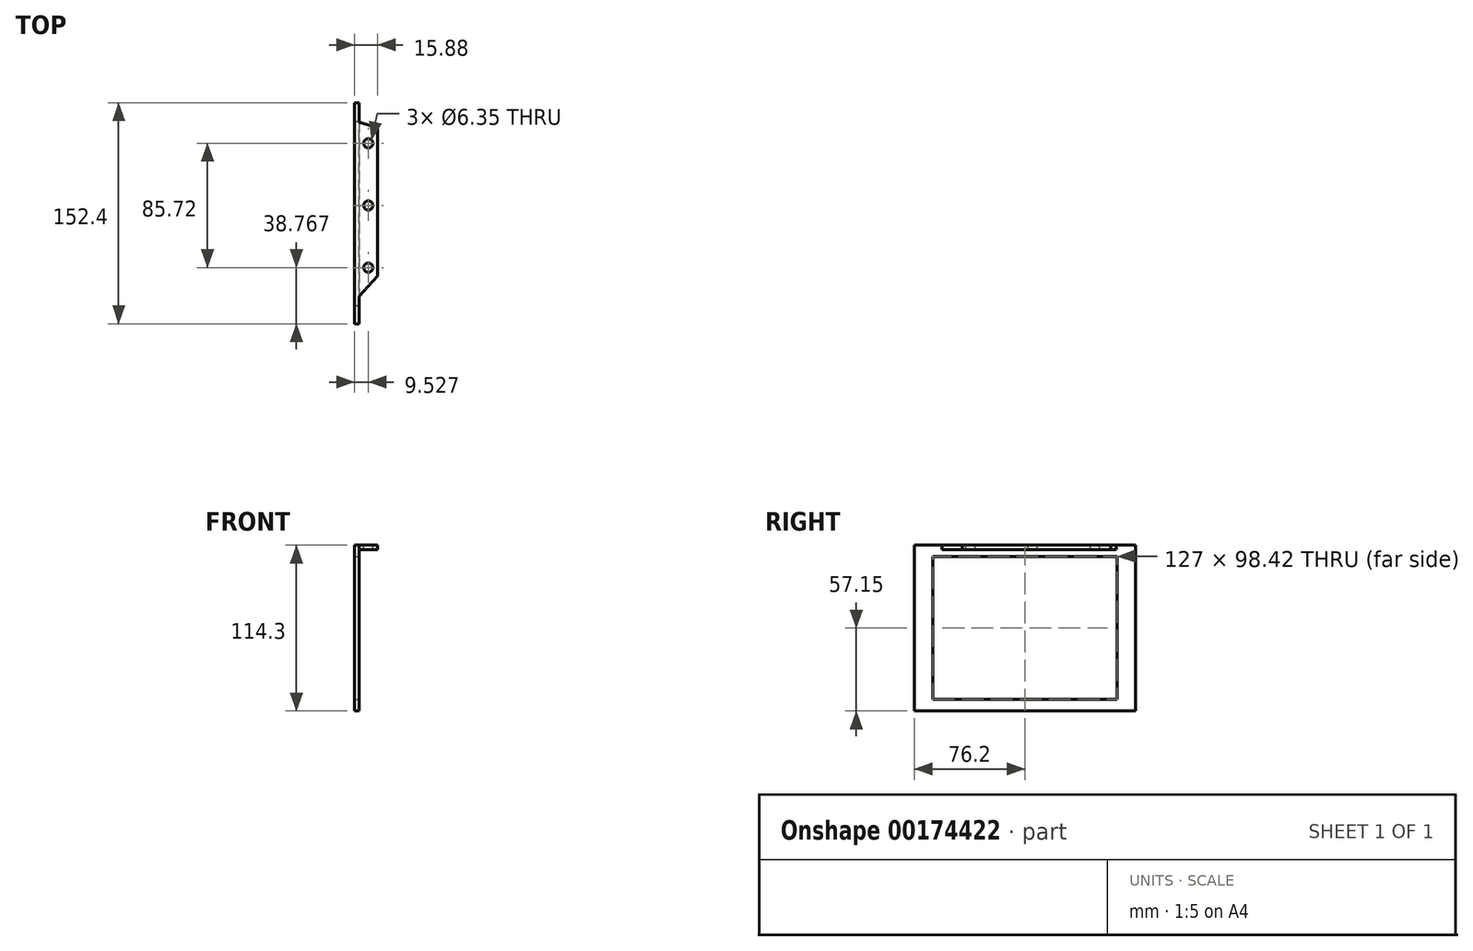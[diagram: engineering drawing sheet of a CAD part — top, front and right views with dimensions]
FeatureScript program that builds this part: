
annotation { "Feature Type Name" : "Feature", "Feature Type Description" : "" }
export const myFeature = defineFeature(function(context is Context, id is Id, definition is map)
    precondition{}
    {
        {
            var Q0;
            Q0=qCreatedBy(makeId("Top.planeOp"),FACE);
            var sketch = newSketch(context, id + "F0", { "sketchPlane" : qUnion([Q0])});
            skLineSegment(sketch, "E0.bottom", {"start": v(1.59, -76.2) * mm, "end": v(-1.59, -76.2) * mm});
            skLineSegment(sketch, "E0.top", {"start": v(1.59, 76.2) * mm, "end": v(-1.59, 76.2) * mm});
            skLineSegment(sketch, "E0.left", {"start": v(1.59, -76.2) * mm, "end": v(1.59, 76.2) * mm});
            skLineSegment(sketch, "E0.right", {"start": v(-1.59, -76.2) * mm, "end": v(-1.59, 76.2) * mm});
            skPoint(sketch, "E0.middle", {"position": v(0, 0) * mm});
            skSolve(sketch);
        }
        {
            var Q0;
            Q0=qSketchRegion(id+"F0",true);
            extrude(context, id + "F1", {"entities" : qUnion([Q0]), "depth" : 114.3 * mm});
        }
        {
            var Q0;
            Q0=makeQuery(id+"F1.opExtrude","SWEPT_FACE",FACE,{"disambiguationData":[OSD([sQuery(id+"F0.wireOp",EDGE,"E0.left")])]});
            var sketch = newSketch(context, id + "F2", { "sketchPlane" : qUnion([Q0])});
            skLineSegment(sketch, "E1.bottom", {"start": v(63.5, 106.36) * mm, "end": v(-63.5, 106.36) * mm});
            skLineSegment(sketch, "E1.top", {"start": v(63.5, 7.94) * mm, "end": v(-63.5, 7.94) * mm});
            skLineSegment(sketch, "E1.left", {"start": v(63.5, 106.36) * mm, "end": v(63.5, 7.94) * mm});
            skLineSegment(sketch, "E1.right", {"start": v(-63.5, 106.36) * mm, "end": v(-63.5, 7.94) * mm});
            skPoint(sketch, "E1.middle", {"position": v(0, 57.15) * mm});
            skPoint(sketch, "E1.middle.positionSnap0", {"position": v(-76.2, 57.15) * mm});
            skPoint(sketch, "E1.centerSnap0", {"position": v(-76.2, 57.15) * mm});
            skSolve(sketch);
        }
        {
            var Q0;
            Q0=qSketchRegion(id+"F2",true);
            extrude(context, id + "F3", {"entities" : qUnion([Q0]), "operationType" : NewBodyOperationType.REMOVE, "oppositeDirection" : true, "depth" : 25.4 * mm});
        }
        {
            var Q0;
            Q0=makeQuery(id+"F1.opExtrude","SWEPT_FACE",FACE,{"disambiguationData":[OSD([sQuery(id+"F0.wireOp",EDGE,"E0.left")])]});
            var sketch = newSketch(context, id + "F4", { "sketchPlane" : qUnion([Q0])});
            skPoint(sketch, "E2", {"position": v(-57.06, 114.3) * mm});
            skPoint(sketch, "E3", {"position": v(62.87, 114.3) * mm});
            skLineSegment(sketch, "E4.bottom", {"start": v(62.87, 114.3) * mm, "end": v(-57.06, 114.3) * mm});
            skLineSegment(sketch, "E4.top", {"start": v(62.87, 111.13) * mm, "end": v(-57.06, 111.12) * mm});
            skLineSegment(sketch, "E4.left", {"start": v(62.87, 114.3) * mm, "end": v(62.87, 111.13) * mm});
            skLineSegment(sketch, "E4.right", {"start": v(-57.06, 114.3) * mm, "end": v(-57.06, 111.13) * mm});
            skSolve(sketch);
        }
        {
            var Q0;
            Q0 = qSketchRegion(id + "F4", true);
            extrude(context, id + "F5", {"entities" : qUnion([Q0]), "operationType" : NewBodyOperationType.ADD, "depth" : 12.7 * mm, "offsetDistance" : 25.4 * mm});
        }
        {
            var Q0;
            Q0=makeQuery(id+"F5.boolean.opBoolean","MERGE",FACE,{"derivedFrom":[makeQuery(id+"F1.opExtrude","CAP_FACE",FACE,{"disambiguationData":[OSD([sQuery(id+"F0.wireOp",EDGE,"E0.bottom"),sQuery(id+"F0.wireOp",EDGE,"E0.top"),sQuery(id+"F0.wireOp",EDGE,"E0.left"),sQuery(id+"F0.wireOp",EDGE,"E0.right")])],"isStart":false}),makeQuery(id+"F5.opExtrude","SWEPT_FACE",FACE,{"disambiguationData":[OSD([sQuery(id+"F4.wireOp",EDGE,"E4.bottom")])]})]});
            var sketch = newSketch(context, id + "F6", { "sketchPlane" : qUnion([Q0])});
            skLineSegment(sketch, "E5", {"start": v(1.59, 62.87) * mm, "end": v(14.29, 59.1) * mm});
            skLineSegment(sketch, "E6", {"start": v(14.29, 59.1) * mm, "end": v(14.29, 62.87) * mm});
            skLineSegment(sketch, "E7", {"start": v(14.29, 62.87) * mm, "end": v(1.59, 62.87) * mm});
            skLineSegment(sketch, "E8", {"start": v(1.59, -57.06) * mm, "end": v(14.29, -43.2) * mm});
            skLineSegment(sketch, "E9", {"start": v(14.29, -43.2) * mm, "end": v(14.29, -57.06) * mm});
            skLineSegment(sketch, "E10", {"start": v(14.29, -57.06) * mm, "end": v(1.59, -57.06) * mm});
            skSolve(sketch);
        }
        {
            var Q0;
            Q0 = qSketchRegion(id + "F6", true);
            extrude(context, id + "F7", {"entities" : qUnion([Q0]), "operationType" : NewBodyOperationType.REMOVE, "oppositeDirection" : true, "depth" : 25.4 * mm, "offsetDistance" : 25.4 * mm});
        }
        {
            var Q0;
            Q0=makeQuery(id+"F5.boolean.opBoolean","MERGE",FACE,{"derivedFrom":[makeQuery(id+"F1.opExtrude","CAP_FACE",FACE,{"disambiguationData":[OSD([sQuery(id+"F0.wireOp",EDGE,"E0.bottom"),sQuery(id+"F0.wireOp",EDGE,"E0.top"),sQuery(id+"F0.wireOp",EDGE,"E0.left"),sQuery(id+"F0.wireOp",EDGE,"E0.right")])],"isStart":false}),makeQuery(id+"F5.opExtrude","SWEPT_FACE",FACE,{"disambiguationData":[OSD([sQuery(id+"F4.wireOp",EDGE,"E4.bottom")])]})]});
            var sketch = newSketch(context, id + "F8", { "sketchPlane" : qUnion([Q0])});
            skLineSegment(sketch, "E11", {"start": v(7.94, 60.99) * mm, "end": v(7.94, -50.13) * mm});
            skCircle(sketch, "E12", {"center": v(7.94, 5.43) * mm, "radius": 3.18 * mm});
            skCircle(sketch, "E13", {"center": v(7.94, 48.29) * mm, "radius": 3.18 * mm});
            skCircle(sketch, "E14", {"center": v(7.94, -37.43) * mm, "radius": 3.18 * mm});
            skSolve(sketch);
        }
        {
            var Q0;
            Q0 = qSketchRegion(id + "F8", true);
            extrude(context, id + "F9", {"entities" : qUnion([Q0]), "operationType" : NewBodyOperationType.REMOVE, "oppositeDirection" : true, "depth" : 25.4 * mm, "offsetDistance" : 25.4 * mm});
        }
    });
